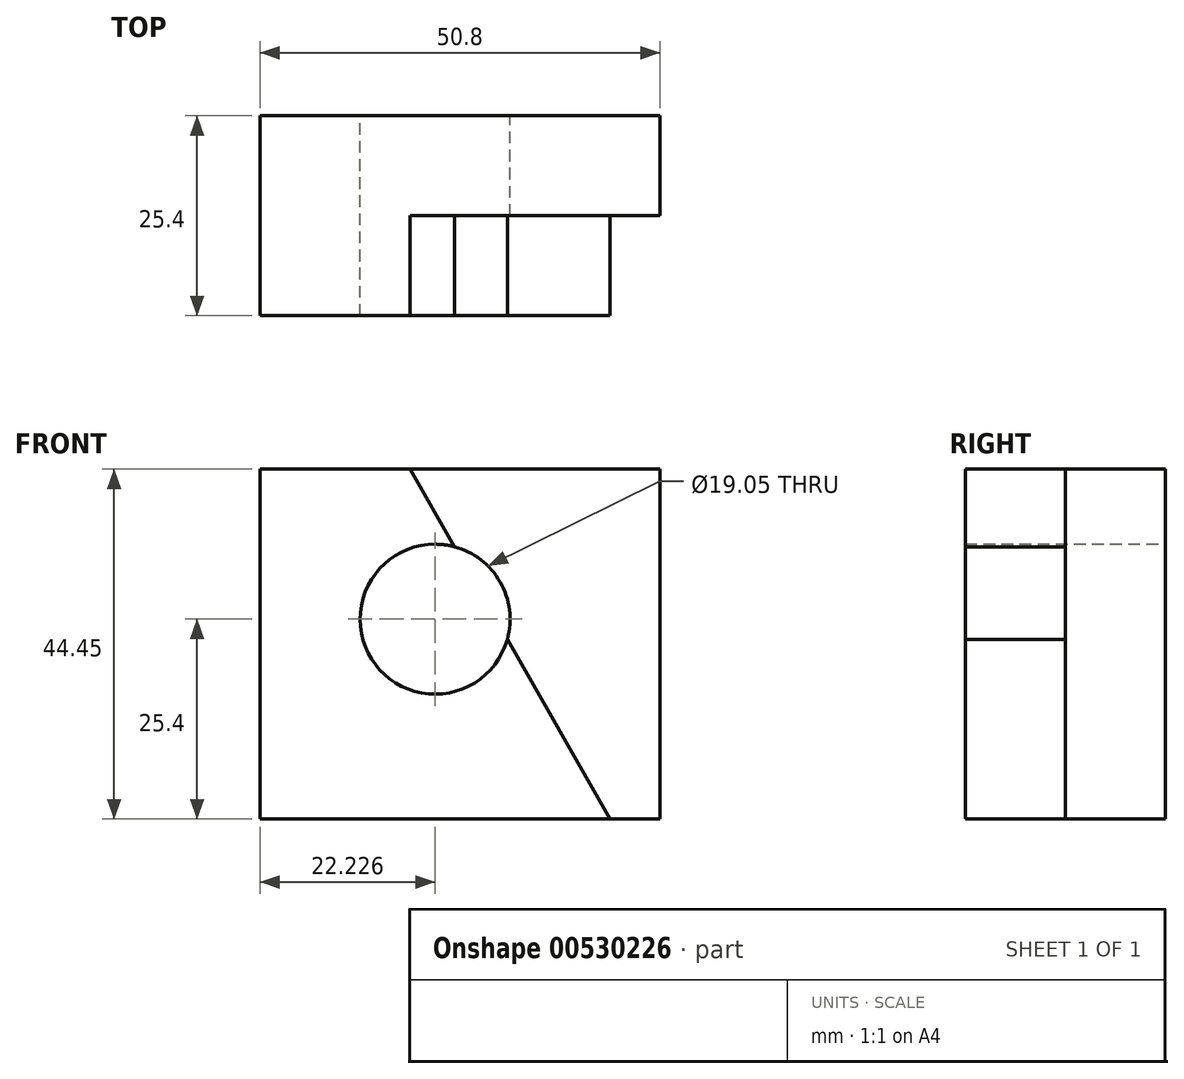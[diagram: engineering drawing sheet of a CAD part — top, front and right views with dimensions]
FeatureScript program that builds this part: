
annotation { "Feature Type Name" : "Feature", "Feature Type Description" : "" }
export const myFeature = defineFeature(function(context is Context, id is Id, definition is map)
    precondition{}
    {
        {
            var Q0;
            Q0=qCreatedBy(makeId("Front.planeOp"),FACE);
            var sketch = newSketch(context, id + "F0", { "sketchPlane" : qUnion([Q0])});
            skLineSegment(sketch, "E0", {"start": v(-45.35, 0) * mm, "end": v(-64.4, 0) * mm});
            skLineSegment(sketch, "E1", {"start": v(-64.4, 0) * mm, "end": v(-64.4, 44.45) * mm});
            skLineSegment(sketch, "E2", {"start": v(-64.4, 44.45) * mm, "end": v(-45.35, 44.45) * mm});
            skLineSegment(sketch, "E3", {"start": v(-45.35, 44.45) * mm, "end": v(-45.35, 0) * mm});
            skSolve(sketch);
        }
        {
            var Q0;
            Q0 = qSketchRegion(id + "F0", true);
            var Q1;
            Q1=makeQuery(id+"F0.imprint","IMPRINT",FACE,{"disambiguationData":[TD([[makeQuery(id+"F0.imprint","IMPRINT",EDGE,{"derivedFrom":sQuery(id+"F0.wireOp",EDGE,"E0")}),-1.0]])]});
            extrude(context, id + "F1", {"entities" : qUnion([Q0, Q1]), "depth" : 25.4 * mm, "offsetDistance" : 25.4 * mm});
        }
        {
            var Q0;
            Q0=makeQuery(id+"F1.opExtrude","SWEPT_FACE",FACE,{"disambiguationData":[OSD([sQuery(id+"F0.wireOp",EDGE,"E3")])]});
            var sketch = newSketch(context, id + "F2", { "sketchPlane" : qUnion([Q0])});
            skLineSegment(sketch, "E4", {"start": v(-12.7, 44.45) * mm, "end": v(-12.7, 0) * mm});
            skLineSegment(sketch, "E5", {"start": v(-12.7, 0) * mm, "end": v(-25.4, 0) * mm});
            skLineSegment(sketch, "E6", {"start": v(-25.4, 0) * mm, "end": v(-25.4, 44.45) * mm});
            skLineSegment(sketch, "E7", {"start": v(-25.4, 44.45) * mm, "end": v(-12.7, 44.45) * mm});
            skSolve(sketch);
        }
        {
            var Q0;
            Q0=makeQuery(id+"F2.imprint","IMPRINT",FACE,{"disambiguationData":[TD([[makeQuery(id+"F2.imprint","IMPRINT",EDGE,{"derivedFrom":sQuery(id+"F2.wireOp",EDGE,"E4")}),-1.0]])]});
            extrude(context, id + "F3", {"entities" : qUnion([Q0]), "operationType" : NewBodyOperationType.ADD, "depth" : 25.4 * mm, "offsetDistance" : 25.4 * mm});
        }
        {
            var Q0;
            Q0=makeQuery(id+"F3.opExtrude","SWEPT_FACE",FACE,{"disambiguationData":[OSD([sQuery(id+"F2.wireOp",EDGE,"E4")])]});
            var sketch = newSketch(context, id + "F4", { "sketchPlane" : qUnion([Q0])});
            skLineSegment(sketch, "E8", {"start": v(45.35, 44.45) * mm, "end": v(19.95, 0) * mm});
            skSolve(sketch);
        }
        {
            var Q0;
            Q0 = qSketchRegion(id + "F4", true);
            var Q1;
            Q1=makeQuery(id+"F4.imprint","IMPRINT",FACE,{"disambiguationData":[TD([[makeQuery(id+"F4.imprint","IMPRINT",EDGE,{"derivedFrom":sQuery(id+"F4.wireOp",EDGE,"E8")}),-1.0]])]});
            extrude(context, id + "F5", {"entities" : qUnion([Q0, Q1]), "operationType" : NewBodyOperationType.REMOVE, "oppositeDirection" : true, "depth" : 25.4 * mm, "offsetDistance" : 25.4 * mm});
        }
        {
            var Q0;
            Q0=makeQuery(id+"F1.opExtrude","SWEPT_FACE",FACE,{"disambiguationData":[OSD([sQuery(id+"F0.wireOp",EDGE,"E3")])]});
            var sketch = newSketch(context, id + "F6", { "sketchPlane" : qUnion([Q0])});
            skLineSegment(sketch, "E9", {"start": v(-12.7, 44.45) * mm, "end": v(-12.7, 0) * mm});
            skLineSegment(sketch, "E10", {"start": v(-12.7, 0) * mm, "end": v(0, 0) * mm});
            skLineSegment(sketch, "E11", {"start": v(0, 0) * mm, "end": v(0, 44.45) * mm});
            skLineSegment(sketch, "E12", {"start": v(0, 44.45) * mm, "end": v(-12.7, 44.45) * mm});
            skSolve(sketch);
        }
        {
            var Q0;
            Q0 = qSketchRegion(id + "F6", true);
            extrude(context, id + "F7", {"entities" : qUnion([Q0]), "operationType" : NewBodyOperationType.ADD, "depth" : 31.75 * mm, "offsetDistance" : 25.4 * mm});
        }
        {
            var Q0;
            Q0=makeQuery(id+"F7.boolean.opBoolean","MERGE",FACE,{"derivedFrom":[makeQuery(id+"F1.opExtrude","CAP_FACE",FACE,{"disambiguationData":[OSD([sQuery(id+"F0.wireOp",EDGE,"E0"),sQuery(id+"F0.wireOp",EDGE,"E1"),sQuery(id+"F0.wireOp",EDGE,"E2"),sQuery(id+"F0.wireOp",EDGE,"E3")])],"isStart":true}),makeQuery(id+"F7.opExtrude","SWEPT_FACE",FACE,{"disambiguationData":[OSD([sQuery(id+"F6.wireOp",EDGE,"E11")])]})]});
            var sketch = newSketch(context, id + "F8", { "sketchPlane" : qUnion([Q0])});
            skCircle(sketch, "E13", {"center": v(42.17, 25.4) * mm, "radius": 9.52 * mm});
            skSolve(sketch);
        }
        {
            var Q0;
            Q0 = qSketchRegion(id + "F8", true);
            var Q1;
            Q1=makeQuery(id+"F8.imprint","IMPRINT",FACE,{"disambiguationData":[TD([[makeQuery(id+"F8.imprint","IMPRINT",EDGE,{"derivedFrom":sQuery(id+"F8.wireOp",EDGE,"E13")}),1.0]])]});
            extrude(context, id + "F9", {"entities" : qUnion([Q0, Q1]), "operationType" : NewBodyOperationType.REMOVE, "oppositeDirection" : true, "depth" : 25.4 * mm, "offsetDistance" : 25.4 * mm});
        }
    });
